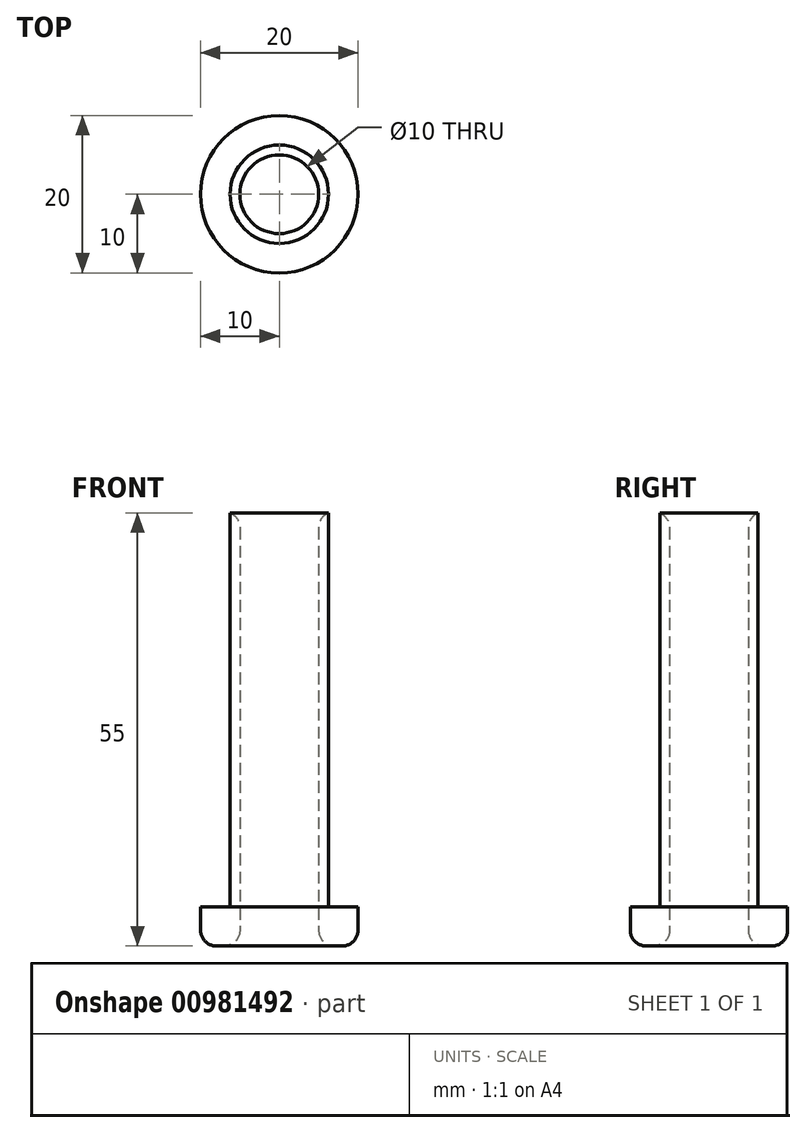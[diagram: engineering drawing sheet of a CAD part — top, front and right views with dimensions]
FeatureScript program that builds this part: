
annotation { "Feature Type Name" : "Feature", "Feature Type Description" : "" }
export const myFeature = defineFeature(function(context is Context, id is Id, definition is map)
    precondition{}
    {
        {
            var Q0;
            Q0=qCreatedBy(makeId("Top.planeOp"),FACE);
            var sketch = newSketch(context, id + "F0", { "sketchPlane" : qUnion([Q0])});
            skCircle(sketch, "E0", {"center": v(0, 0) * mm, "radius": 10 * mm});
            skCircle(sketch, "E1", {"center": v(0, 0) * mm, "radius": 6.25 * mm});
            skCircle(sketch, "E2", {"center": v(0, 0) * mm, "radius": 5 * mm});
            skSolve(sketch);
        }
        {
            var Q0;
            Q0=makeQuery(id+"F0.imprint","IMPRINT",FACE,{"disambiguationData":[TD([[makeQuery(id+"F0.imprint","IMPRINT",EDGE,{"derivedFrom":sQuery(id+"F0.wireOp",EDGE,"E0")}),1.0]])]});
            extrude(context, id + "F1", {"entities" : qUnion([Q0]), "depth" : 5 * mm, "offsetDistance" : 25 * mm});
        }
        {
            var Q0;
            Q0=makeQuery(id+"F0.imprint","IMPRINT",FACE,{"disambiguationData":[TD([[makeQuery(id+"F0.imprint","IMPRINT",EDGE,{"derivedFrom":sQuery(id+"F0.wireOp",EDGE,"E1")}),1.0]])]});
            extrude(context, id + "F2", {"entities" : qUnion([Q0]), "operationType" : NewBodyOperationType.ADD, "depth" : 55 * mm, "offsetDistance" : 25 * mm});
        }
        {
            var Q0;
            Q0=makeQuery(id+"F0.imprint","IMPRINT",FACE,{"disambiguationData":[TD([[makeQuery(id+"F0.imprint","IMPRINT",EDGE,{"derivedFrom":sQuery(id+"F0.wireOp",EDGE,"E2")}),1.0]])]});
            extrude(context, id + "F3", {"entities" : qUnion([Q0]), "operationType" : NewBodyOperationType.REMOVE, "depth" : 51 * mm, "offsetDistance" : 25 * mm});
        }
        {
            var Q0;
            Q0=makeQuery(id+"F2.opExtrude","CAP_EDGE",EDGE,{"disambiguationData":[OSD([sQuery(id+"F0.wireOp",EDGE,"E2")])],"isStart":true});
            var Q1;
            Q1=makeQuery(id+"F2.opExtrude","CAP_EDGE",EDGE,{"disambiguationData":[OSD([sQuery(id+"F0.wireOp",EDGE,"E2")])],"isStart":false});
            var Q2;
            Q2=makeQuery(id+"F1.opExtrude","CAP_EDGE",EDGE,{"disambiguationData":[OSD([sQuery(id+"F0.wireOp",EDGE,"E0")])],"isStart":true});
            fillet(context, id + "F4", {"entities" : qUnion([Q0, Q1, Q2]), "radius" : 2 * mm, "tangentPropagation" : true, "allowEdgeOverflow" : false});
        }
    });
